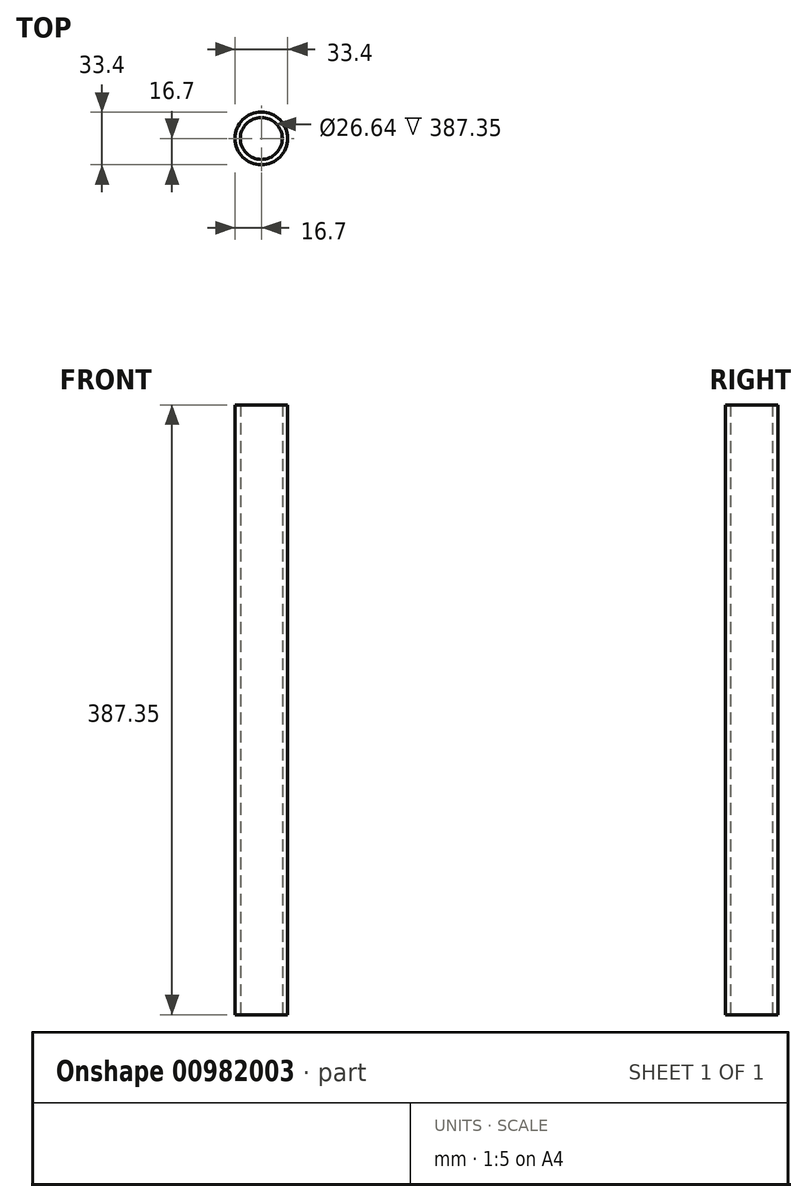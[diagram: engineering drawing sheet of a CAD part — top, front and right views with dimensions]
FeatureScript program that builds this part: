
annotation { "Feature Type Name" : "Feature", "Feature Type Description" : "" }
export const myFeature = defineFeature(function(context is Context, id is Id, definition is map)
    precondition{}
    {
        {
            var Q0;
            Q0=qCreatedBy(makeId("Top.planeOp"),FACE);
            var sketch = newSketch(context, id + "F0", { "sketchPlane" : qUnion([Q0])});
            skCircle(sketch, "E0", {"center": v(0, 0) * mm, "radius": 13.32 * mm});
            skCircle(sketch, "E1", {"center": v(0, 0) * mm, "radius": 16.7 * mm});
            skSolve(sketch);
        }
        {
            var Q0;
            Q0=qSketchRegion(id+"F0",true);
            extrude(context, id + "F1", {"entities" : qUnion([Q0]), "depth" : 387.35 * mm, "offsetDistance" : 25.4 * mm});
        }
    });
